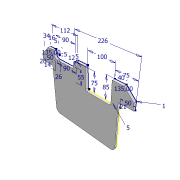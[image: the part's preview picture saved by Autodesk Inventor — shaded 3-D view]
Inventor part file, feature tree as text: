
AUTODESK INVENTOR PART (.ipt)
format: ipt  version: 2020 (Build 240168000, 168)  size: 216,064 bytes
history: native  units: mm
features: extrude x4, sketch x4, projected_geometry x3, chamfer x2, plane x1, direct_edit x1, move_body x1
ambient origin geometry x8: Origin, YZ Plane, XZ Plane, XY Plane, X Axis, Y Axis, Z Axis, Center Point
bodies: Solid1 (feature_tree)
feature tree (16):
  extrude  "Extrusion1"  Depth=168.0mm
  extrude  "Extrusion2"  Depth=10.0mm TaperAngle=0.0deg
  chamfer  "Chamfer2"  Distance=85.0mm
  chamfer  "Chamfer3"  Distance=75.0mm
  extrude  "Extrusion3"  TaperAngle=135.0deg  [1 undecoded]
  plane  "Work Plane1"
  extrude  "Extrusion4"  Depth=10.0mm
  direct_edit  "Direct Edit1"
  sketch  "Sketch1"  dims[d0=278.0mm d1=168.0mm]
  sketch  "Sketch2"  dims[d2=19.0mm d3=10.0mm d4=0.0mm]
  projected_geometry  "Projected Loop1"
  sketch  "Sketch3"  dims[d8=21.0mm]
  projected_geometry  "Projected Loop2"
  projected_geometry  "Projected Loop3"
  sketch  "Sketch4"  dims[d9=50.0mm d10=85.0mm d11=75.0mm d12=135.0deg d13=40.0mm d14=100.0mm d16=90.0mm d17=50.0mm d19=34.0mm d20=135.0deg d21=5.0mm d22=1.0mm d23=14.0mm d24=5.0mm d26=90.0mm d29=12.0mm d30=226.0mm d31=5.0mm d32=5.0mm d33=55.0mm d34=20.0mm d35=16.0mm d36=75.0mm d37=112.0mm d38=26.0mm d39=10.0mm d40=0.0mm d41=4.0mm d42=2.0mm d43=45.0deg d44=4.0mm d45=2.0mm d46=45.0deg d47=45.0deg d48=4.0mm d49=10.0mm d50=0.0mm d51=10.0mm d52=0.0mm d53=0.0mm d54=0.0mm d55=-1.0mm]
  move_body  "Move1"
note: 1 required parameter value undecoded (feature->parameter linkage not recoverable at this tier; creation-order binding heuristic only, values carry confidence <= 0.55)
